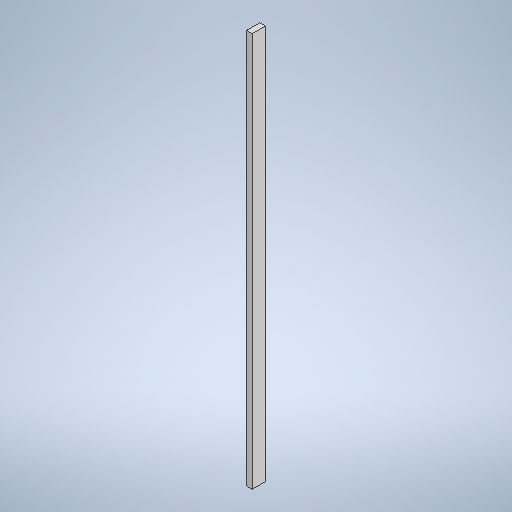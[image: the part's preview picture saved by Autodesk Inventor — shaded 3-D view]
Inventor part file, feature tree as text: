
AUTODESK INVENTOR PART (.ipt)
format: ipt  version: 2025 (Build 290162000, 162)  size: 252,928 bytes
history: native  units: in
note: dims shown in document units (in); Inventor stores cm internally (conversion verified against a paired STEP export)
features: extrude x1, sketch x1
ambient origin geometry x8: Origin, YZ Plane, XZ Plane, XY Plane, X Axis, Y Axis, Z Axis, Center Point
bodies: Solid1 (feature_tree)
feature tree (2):
  extrude  "Extrusion1"  Depth=3.5in
  sketch  "Sketch1"  dims[d0=105.0in d1=3.5in d2=1.5in d3=0.0in]
